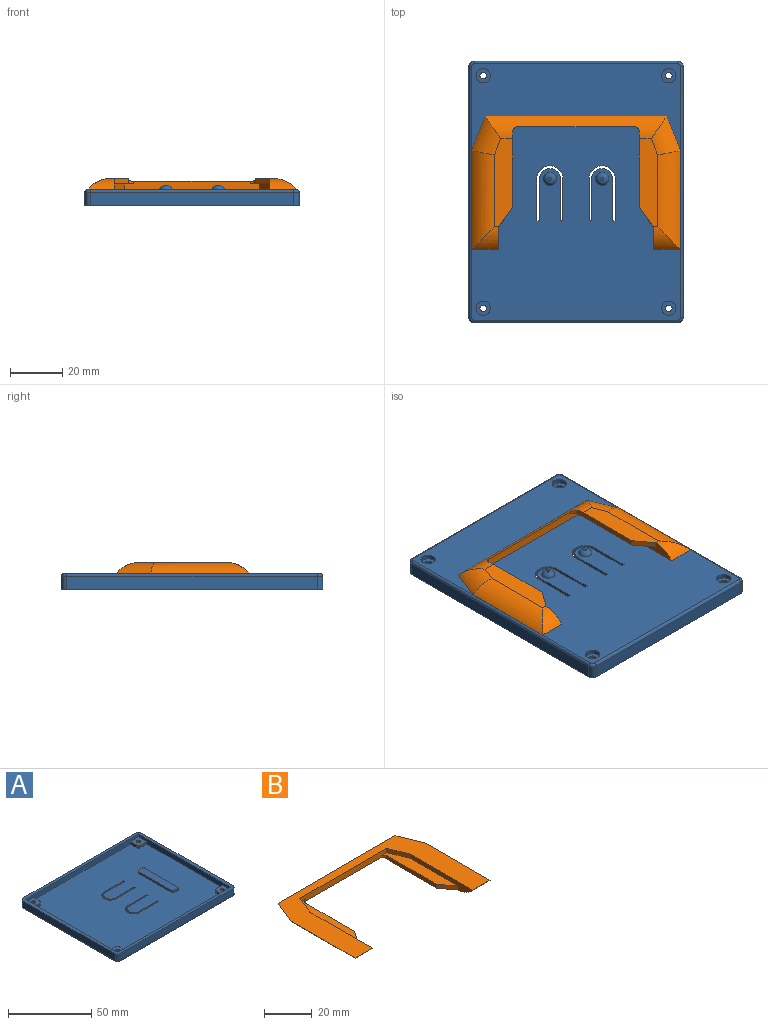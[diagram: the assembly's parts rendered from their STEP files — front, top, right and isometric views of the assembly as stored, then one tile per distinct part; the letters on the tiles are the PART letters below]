
ASSEMBLY  parts=2 mates=1
PART A: 80 faces, bbox 100.3x82.3x7.5 mm
  f0: plane 96x78mm, normal (0,0,1), area 7054mm2, adj f5,f6,f16,f17,f19,f20,f21,f23
  f1: cylinder r=1.25mm len=2.5mm, axis (0,0,-1), area 18.8mm2, adj f34,f41
  f2: cylinder r=1.25mm len=2.5mm, axis (0,0,-1), area 18.8mm2, adj f30,f39
  f3: cylinder r=1.25mm len=2.5mm, axis (0,0,-1), area 18.8mm2, adj f26,f37
  f4: cylinder r=1.25mm len=2.5mm, axis (0,0,-1), area 18.8mm2, adj f22,f35
  f5: plane 96x4mm, normal (0,-1,0), area 356mm2, adj f0,f6,f17,f18,f23,f26,f31,f34
  f6: plane 78x4mm, normal (1,0,0), area 284mm2, adj f0,f5,f16,f18,f21,f22,f24,f26
  f7: plane 96x5mm, normal (0,1,0), area 480mm2, adj f8,f14,f18,f43
  f8: cylinder r=2mm len=5mm, axis (0,0,-1), area 15.7mm2, adj f7,f9,f18,f44
  f9: plane 78x5mm, normal (-1,0,0), area 390mm2, adj f8,f10,f18,f46
  f10: cylinder r=2mm len=5mm, axis (0,0,-1), area 15.7mm2, adj f9,f11,f18,f48
  f11: plane 96x5mm, normal (0,-1,0), area 480mm2, adj f10,f12,f18,f50
  f12: cylinder r=2mm len=5mm, axis (0,0,-1), area 15.7mm2, adj f11,f13,f18,f49
  f13: plane 78x5mm, normal (1,0,0), area 390mm2, adj f12,f14,f18,f47
  f14: cylinder r=2mm len=5mm, axis (0,0,-1), area 15.7mm2, adj f7,f13,f18,f45
  f15: plane 98x80mm, normal (0,0,-1), area 7612.6mm2, adj f36,f38,f40,f42,f43,f44,f45,f46
  f16: plane 96x4mm, normal (0,1,0), area 356mm2, adj f0,f6,f17,f18,f19,f22,f27,f30
  f17: plane 78x4mm, normal (-1,0,0), area 284mm2, adj f0,f5,f16,f18,f28,f30,f33,f34
  f18: plane 100x82mm, normal (0,0,1), area 708.6mm2, adj f5,f6,f7,f8,f9,f10,f11,f12
  f19: plane 5x2mm, normal (1,0,0), area 10mm2, adj f0,f16,f20,f22
  f20: cylinder r=2mm len=2mm, axis (0,0,-1), area 6.3mm2, adj f0,f19,f21,f22
  f21: plane 5x2mm, normal (0,1,0), area 10mm2, adj f0,f6,f20,f22
  f22: plane 7x7mm, normal (0,0,1), area 43.2mm2, adj f4,f6,f16,f19,f20,f21
  f23: plane 5x2mm, normal (1,0,0), area 10mm2, adj f0,f5,f25,f26
  f24: plane 5x2mm, normal (0,-1,0), area 10mm2, adj f0,f6,f25,f26
  f25: cylinder r=2mm len=2mm, axis (0,0,-1), area 6.3mm2, adj f0,f23,f24,f26
  f26: plane 7x7mm, normal (0,0,1), area 43.2mm2, adj f3,f5,f6,f23,f24,f25
  f27: plane 5x2mm, normal (-1,0,0), area 10mm2, adj f0,f16,f29,f30
  f28: plane 5x2mm, normal (0,1,0), area 10mm2, adj f0,f17,f29,f30
  f29: cylinder r=2mm len=2mm, axis (0,0,-1), area 6.3mm2, adj f0,f27,f28,f30
  f30: plane 7x7mm, normal (0,0,1), area 43.2mm2, adj f2,f16,f17,f27,f28,f29
  f31: plane 5x2mm, normal (-1,0,0), area 10mm2, adj f0,f5,f32,f34
  f32: cylinder r=2mm len=2mm, axis (0,0,-1), area 6.3mm2, adj f0,f31,f33,f34
  f33: plane 5x2mm, normal (0,-1,0), area 10mm2, adj f0,f17,f32,f34
  f34: plane 7x7mm, normal (0,0,1), area 43.2mm2, adj f1,f5,f17,f31,f32,f33
  f35: plane 5.5x5.5mm, normal (0,0,-1), area 18.8mm2, adj f4,f36
  f36: cylinder r=2.75mm len=5.5mm, axis (0,0,-1), area 27.6mm2, adj f15,f35
  f37: plane 5.5x5.5mm, normal (0,0,-1), area 18.8mm2, adj f3,f38
  f38: cylinder r=2.75mm len=5.5mm, axis (0,0,-1), area 27.6mm2, adj f15,f37
  f39: plane 5.5x5.5mm, normal (0,0,-1), area 18.8mm2, adj f2,f40
  f40: cylinder r=2.75mm len=5.5mm, axis (0,0,-1), area 27.6mm2, adj f15,f39
  f41: plane 5.5x5.5mm, normal (0,0,-1), area 18.8mm2, adj f1,f42
  f42: cylinder r=2.75mm len=5.5mm, axis (0,0,-1), area 27.6mm2, adj f15,f41
  f43: cylinder r=1mm len=96mm, axis (-1,0,0), area 150.8mm2, adj f7,f15,f44,f45
  f44: torus R=1mm, axis (0,0,1), area 4mm2, adj f8,f15,f43,f46
  f45: torus R=1mm, axis (0,0,1), area 4mm2, adj f14,f15,f43,f47
  f46: cylinder r=1mm len=78mm, axis (0,-1,0), area 122.5mm2, adj f9,f15,f44,f48
  f47: cylinder r=1mm len=78mm, axis (0,1,0), area 122.5mm2, adj f13,f15,f45,f49
  f48: torus R=1mm, axis (0,0,1), area 4mm2, adj f10,f15,f46,f50
  f49: torus R=1mm, axis (0,0,1), area 4mm2, adj f12,f15,f47,f50
  f50: cylinder r=1mm len=96mm, axis (1,0,0), area 150.8mm2, adj f11,f15,f48,f49
  f51: cylinder r=5mm len=10mm, axis (0,0,-1), area 31.4mm2, adj f0,f15,f52,f58
  f52: plane 16x2mm, normal (0,-1,0), area 32mm2, adj f0,f15,f51,f53
  f53: plane 2x1mm, normal (-1,0,0), area 2mm2, adj f0,f15,f52,f54
  f54: plane 16x2mm, normal (0,1,0), area 32mm2, adj f0,f15,f53,f55
  f55: cylinder r=4mm len=8mm, axis (0,0,-1), area 25.1mm2, adj f0,f15,f54,f56
  f56: plane 16x2mm, normal (0,-1,0), area 32mm2, adj f0,f15,f55,f57
  f57: plane 2x1mm, normal (-1,0,0), area 2mm2, adj f0,f15,f56,f58
  f58: plane 16x2mm, normal (0,1,0), area 32mm2, adj f0,f15,f51,f57
  f59: cylinder r=5mm len=10mm, axis (0,0,-1), area 31.4mm2, adj f0,f15,f60,f66
  f60: plane 16x2mm, normal (0,-1,0), area 32mm2, adj f0,f15,f59,f61
  f61: plane 2x1mm, normal (-1,0,0), area 2mm2, adj f0,f15,f60,f62
  f62: plane 16x2mm, normal (0,1,0), area 32mm2, adj f0,f15,f61,f63
  f63: cylinder r=4mm len=8mm, axis (0,0,-1), area 25.1mm2, adj f0,f15,f62,f64
  f64: plane 16x2mm, normal (0,-1,0), area 32mm2, adj f0,f15,f63,f65
  f65: plane 2x1mm, normal (-1,0,0), area 2mm2, adj f0,f15,f64,f66
  f66: plane 16x2mm, normal (0,1,0), area 32mm2, adj f0,f15,f59,f65
  f67: plane 1.13x1.13mm, normal (0,0,-1), area 1mm2, adj f69
  f68: plane 1.13x1.13mm, normal (0,0,-1), area 1mm2, adj f70
  f69: torus R=0.56mm, axis (0,0,1), area 28.2mm2, adj f15,f67
  f70: torus R=0.56mm, axis (0,0,1), area 28.2mm2, adj f15,f68
  f71: plane 3x1.5mm, normal (0,1,0), area 4.5mm2, adj f0,f72,f78,f79
  f72: cylinder r=1mm len=1.5mm, axis (0,0,-1), area 2.4mm2, adj f0,f71,f73,f79
  f73: plane 28x1.5mm, normal (-1,0,0), area 42mm2, adj f0,f72,f74,f79
  f74: cylinder r=1mm len=1.5mm, axis (0,0,-1), area 2.4mm2, adj f0,f73,f75,f79
  f75: plane 3x1.5mm, normal (0,-1,0), area 4.5mm2, adj f0,f74,f76,f79
  f76: cylinder r=1mm len=1.5mm, axis (0,0,-1), area 2.4mm2, adj f0,f75,f77,f79
  f77: plane 28x1.5mm, normal (1,0,0), area 42mm2, adj f0,f76,f78,f79
  f78: cylinder r=1mm len=1.5mm, axis (0,0,-1), area 2.4mm2, adj f0,f71,f77,f79
  f79: plane 30x5mm, normal (0,0,1), area 149.1mm2, adj f71,f72,f73,f74,f75,f76,f77,f78
PART B: 23 faces, bbox 79.9x51x4.2 mm
  f0: plane 33.71x7.05mm, normal (0,0,-1), area 210.1mm2, adj f1,f2,f17,f18,f19,f20
  f1: plane 7.5x5.5mm, normal (0.81,-0.59,0), area 18.6mm2, adj f0,f2,f4,f14,f18
  f2: plane 29x2mm, normal (1,0,0), area 57.7mm2, adj f0,f1,f3,f4,f17
  f3: cylinder r=2mm len=2mm, axis (0,0,-1), area 3.9mm2, adj f2,f4,f7,f17
  f4: plane 38.5x7.5mm, normal (0,0,1), area 172mm2, adj f1,f2,f3,f6,f7,f14
  f5: plane 33.71x7.05mm, normal (0,0,-1), area 210.1mm2, adj f8,f9,f16,f17,f21,f22
  f6: plane 10x4mm, normal (0.93,-0.37,0), area 23.7mm2, adj f4,f7,f14,f15
  f7: plane 51.5x3.17mm, normal (0,-1,0), area 156.5mm2, adj f3,f4,f6,f10,f11,f13,f15,f17
  f8: plane 29x2mm, normal (-1,0,0), area 57.7mm2, adj f5,f9,f10,f11,f17
  f9: plane 7.5x5.5mm, normal (-0.81,-0.59,0), area 18.6mm2, adj f5,f8,f11,f12,f16
  f10: cylinder r=2mm len=2mm, axis (0,0,-1), area 3.9mm2, adj f7,f8,f11,f17
  f11: plane 38.5x7.5mm, normal (0,0,1), area 172mm2, adj f7,f8,f9,f10,f12,f13
  f12: plane 37x4.2mm, normal (-1,0,0), area 87.4mm2, adj f9,f11,f13,f15,f16
  f13: plane 10x4mm, normal (-0.93,-0.37,0), area 23.7mm2, adj f7,f11,f12,f15
  f14: plane 37x4.2mm, normal (1,0,0), area 87.4mm2, adj f1,f4,f6,f15,f18
  f15: plane 79.9x51mm, normal (0,0,1), area 1248.4mm2, adj f6,f7,f12,f13,f14,f16,f17,f18
  f16: cylinder r=11mm len=10.31mm, axis (1,0,0), area 61.7mm2, adj f5,f9,f12,f15,f22
  f17: cylinder r=11mm len=69.32mm, axis (1,0,0), area 404.9mm2, adj f0,f2,f3,f5,f7,f8,f10,f15
  f18: cylinder r=11mm len=10.31mm, axis (1,0,0), area 61.7mm2, adj f0,f1,f14,f15,f19
  f19: cylinder r=11mm len=37.77mm, axis (0,-1,0), area 328.3mm2, adj f0,f15,f18,f20
  f20: cylinder r=11mm len=16.44mm, axis (-0.37,-0.93,0), area 107.1mm2, adj f0,f15,f17,f19
  f21: cylinder r=11mm len=16.44mm, axis (0.37,-0.93,0), area 107.1mm2, adj f5,f15,f17,f22
  f22: cylinder r=11mm len=37.77mm, axis (0,-1,0), area 328.3mm2, adj f5,f15,f16,f21
PLACE A rot(axis=(0.71,-0.71,0),180deg) t=(39.62,63.5,-4.09)mm
PLACE B rot(axis=(0,1,0),180deg) t=(-1.13,24.25,0.11)mm
MATE fastened B.f15 <-> A.f15  axis (0,0,-1) through (-1.38,38.5,-4.09)mm
